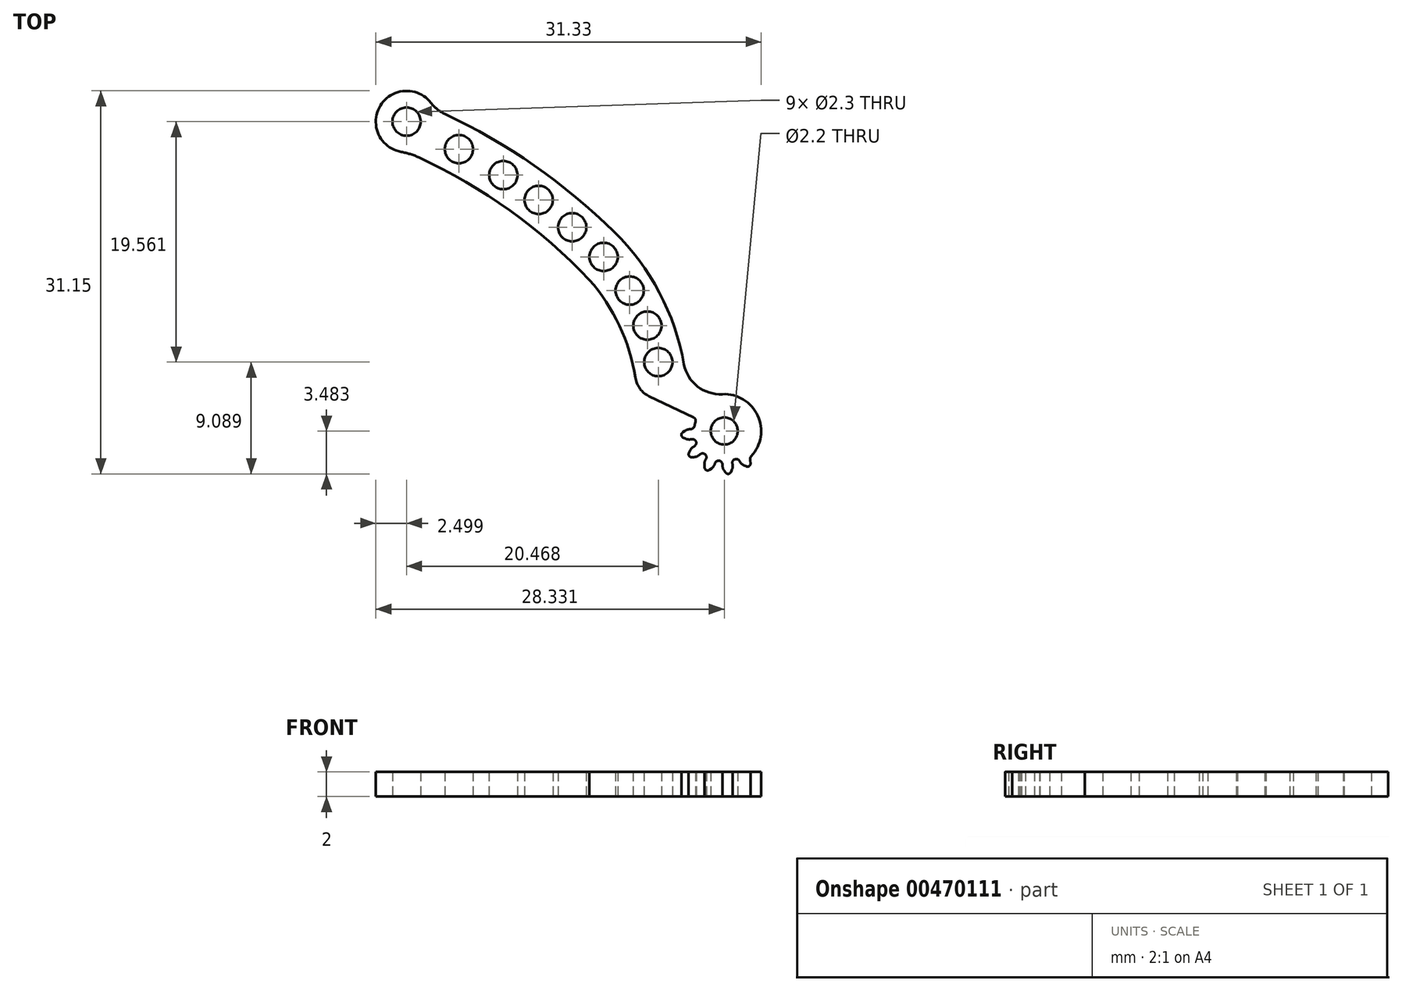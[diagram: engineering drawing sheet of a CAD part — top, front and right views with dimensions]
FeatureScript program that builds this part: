
annotation { "Feature Type Name" : "Feature", "Feature Type Description" : "" }
export const myFeature = defineFeature(function(context is Context, id is Id, definition is map)
    precondition{}
    {
        {
            var Q0;
            Q0=qCreatedBy(makeId("Top.planeOp"),FACE);
            var sketch = newSketch(context, id + "F0", { "sketchPlane" : qUnion([Q0])});
            skCircle(sketch, "E0", {"center": v(1.21, -17.45) * mm, "radius": 1.1 * mm});
            skArc(sketch, "E1", {"start": v(1.58, -20.42) * mm, "mid": v(4.1, -18.23) * mm, "end": v(3.02, -15.06) * mm});
            skArc(sketch, "E2", {"start": v(-0.1, -15.38) * mm, "mid": v(-0.23, -15.47) * mm, "end": v(-0.36, -15.56) * mm});
            skArc(sketch, "E3", {"start": v(4.77, 0.7) * mm, "mid": v(3.26, 9.01) * mm, "end": v(0.37, 16.95) * mm});
            skArc(sketch, "E4", {"start": v(0.1, 18.33) * mm, "mid": v(-3.2, 20.8) * mm, "end": v(-4.32, 16.84) * mm});
            skArc(sketch, "E5", {"start": v(0.1, 18.33) * mm, "mid": v(0.15, 17.62) * mm, "end": v(0.37, 16.95) * mm});
            skArc(sketch, "E6", {"start": v(2.2, -11.17) * mm, "mid": v(4.4, -5.43) * mm, "end": v(4.77, 0.7) * mm});
            skArc(sketch, "E7", {"start": v(2.2, -11.17) * mm, "mid": v(1.88, -13.27) * mm, "end": v(3.02, -15.06) * mm});
            skArc(sketch, "E8", {"start": v(-1.45, -15.36) * mm, "mid": v(-1.57, -15.38) * mm, "end": v(-1.67, -15.46) * mm});
            skArc(sketch, "E9", {"start": v(-0.81, -15.56) * mm, "mid": v(-1.02, -15.43) * mm, "end": v(-1.25, -15.37) * mm});
            skLineSegment(sketch, "E10", {"start": v(-1.25, -15.37) * mm, "end": v(-1.45, -15.36) * mm});
            skArc(sketch, "E11", {"start": v(-0.81, -15.56) * mm, "mid": v(-0.59, -15.64) * mm, "end": v(-0.36, -15.56) * mm});
            skArc(sketch, "E12", {"start": v(-1.67, -15.46) * mm, "mid": v(-1.72, -15.59) * mm, "end": v(-1.7, -15.71) * mm});
            skArc(sketch, "E13", {"start": v(-1.6, -15.9) * mm, "mid": v(-1.46, -16.1) * mm, "end": v(-1.26, -16.25) * mm});
            skLineSegment(sketch, "E14", {"start": v(-1.6, -15.9) * mm, "end": v(-1.7, -15.71) * mm});
            skArc(sketch, "E15", {"start": v(-2.14, -16.97) * mm, "mid": v(-2.23, -17.05) * mm, "end": v(-2.28, -17.17) * mm});
            skArc(sketch, "E16", {"start": v(-1.46, -16.83) * mm, "mid": v(-1.71, -16.81) * mm, "end": v(-1.96, -16.88) * mm});
            skLineSegment(sketch, "E17", {"start": v(-1.96, -16.88) * mm, "end": v(-2.14, -16.97) * mm});
            skArc(sketch, "E18", {"start": v(-2.28, -17.17) * mm, "mid": v(-2.25, -17.3) * mm, "end": v(-2.17, -17.4) * mm});
            skArc(sketch, "E19", {"start": v(-2, -17.51) * mm, "mid": v(-1.78, -17.62) * mm, "end": v(-1.53, -17.64) * mm});
            skLineSegment(sketch, "E20", {"start": v(-2, -17.51) * mm, "end": v(-2.17, -17.4) * mm});
            skArc(sketch, "E21", {"start": v(-1.93, -18.7) * mm, "mid": v(-1.97, -18.83) * mm, "end": v(-1.95, -18.95) * mm});
            skArc(sketch, "E22", {"start": v(-1.41, -18.25) * mm, "mid": v(-1.64, -18.36) * mm, "end": v(-1.82, -18.54) * mm});
            skLineSegment(sketch, "E23", {"start": v(-1.82, -18.54) * mm, "end": v(-1.93, -18.7) * mm});
            skArc(sketch, "E24", {"start": v(-1.95, -18.95) * mm, "mid": v(-1.86, -19.05) * mm, "end": v(-1.74, -19.1) * mm});
            skArc(sketch, "E25", {"start": v(-1.54, -19.11) * mm, "mid": v(-1.3, -19.09) * mm, "end": v(-1.06, -18.98) * mm});
            skLineSegment(sketch, "E26", {"start": v(-1.54, -19.11) * mm, "end": v(-1.74, -19.1) * mm});
            skArc(sketch, "E27", {"start": v(-0.88, -20.1) * mm, "mid": v(-0.86, -20.23) * mm, "end": v(-0.77, -20.33) * mm});
            skArc(sketch, "E28", {"start": v(-0.66, -19.45) * mm, "mid": v(-0.8, -19.66) * mm, "end": v(-0.86, -19.9) * mm});
            skLineSegment(sketch, "E29", {"start": v(-0.86, -19.9) * mm, "end": v(-0.88, -20.1) * mm});
            skArc(sketch, "E30", {"start": v(-0.77, -20.33) * mm, "mid": v(-0.65, -20.37) * mm, "end": v(-0.52, -20.35) * mm});
            skArc(sketch, "E31", {"start": v(-0.34, -20.27) * mm, "mid": v(-0.14, -20.12) * mm, "end": v(0.01, -19.91) * mm});
            skLineSegment(sketch, "E32", {"start": v(-0.34, -20.27) * mm, "end": v(-0.52, -20.35) * mm});
            skArc(sketch, "E33", {"start": v(0.73, -20.8) * mm, "mid": v(0.81, -20.9) * mm, "end": v(0.94, -20.94) * mm});
            skArc(sketch, "E34", {"start": v(0.6, -20.12) * mm, "mid": v(0.58, -20.37) * mm, "end": v(0.64, -20.61) * mm});
            skLineSegment(sketch, "E35", {"start": v(0.64, -20.61) * mm, "end": v(0.73, -20.8) * mm});
            skArc(sketch, "E36", {"start": v(0.94, -20.94) * mm, "mid": v(1.06, -20.91) * mm, "end": v(1.16, -20.83) * mm});
            skArc(sketch, "E37", {"start": v(1.28, -20.66) * mm, "mid": v(1.3, -20.63) * mm, "end": v(1.31, -20.6) * mm});
            skLineSegment(sketch, "E38", {"start": v(1.28, -20.66) * mm, "end": v(1.16, -20.83) * mm});
            skArc(sketch, "E39", {"start": v(1.58, -20.42) * mm, "mid": v(1.42, -20.48) * mm, "end": v(1.31, -20.6) * mm});
            skArc(sketch, "E40", {"start": v(0.6, -20.12) * mm, "mid": v(0.4, -19.76) * mm, "end": v(0.01, -19.91) * mm});
            skArc(sketch, "E41", {"start": v(-0.66, -19.45) * mm, "mid": v(-0.65, -19.04) * mm, "end": v(-1.06, -18.98) * mm});
            skArc(sketch, "E42", {"start": v(-1.41, -18.25) * mm, "mid": v(-1.2, -17.9) * mm, "end": v(-1.53, -17.64) * mm});
            skArc(sketch, "E43", {"start": v(-1.46, -16.83) * mm, "mid": v(-1.1, -16.63) * mm, "end": v(-1.26, -16.25) * mm});
            skCircle(sketch, "E44", {"center": v(-2.4, 18.44) * mm, "radius": 1.15 * mm});
            skLineSegment(sketch, "E45", {"start": v(0, -15) * mm, "end": v(-1.65, -11.36) * mm});
            skArc(sketch, "E46", {"start": v(-0.1, -15.38) * mm, "mid": v(0.02, -15.2) * mm, "end": v(0, -15) * mm});
            skArc(sketch, "E47", {"start": v(-1.53, -9.49) * mm, "mid": v(0.2, -5.4) * mm, "end": v(0.72, -1) * mm});
            skArc(sketch, "E48", {"start": v(-1.53, -9.49) * mm, "mid": v(-1.82, -10.41) * mm, "end": v(-1.65, -11.36) * mm});
            skArc(sketch, "E49", {"start": v(0.72, -1) * mm, "mid": v(-0.62, 7.48) * mm, "end": v(-3.5, 15.56) * mm});
            skArc(sketch, "E50", {"start": v(-3.5, 15.56) * mm, "mid": v(-3.87, 16.22) * mm, "end": v(-4.32, 16.84) * mm});
            skCircle(sketch, "E51", {"center": v(0.7, -9.7) * mm, "radius": 1.15 * mm});
            skCircle(sketch, "E52", {"center": v(1.93, -6.86) * mm, "radius": 1.15 * mm});
            skCircle(sketch, "E53", {"center": v(2.67, -3.75) * mm, "radius": 1.15 * mm});
            skCircle(sketch, "E54", {"center": v(2.8, -0.3) * mm, "radius": 1.15 * mm});
            skCircle(sketch, "E55", {"center": v(2.4, 3.2) * mm, "radius": 1.15 * mm});
            skCircle(sketch, "E56", {"center": v(1.74, 6.65) * mm, "radius": 1.15 * mm});
            skCircle(sketch, "E57", {"center": v(0.83, 10.05) * mm, "radius": 1.15 * mm});
            skCircle(sketch, "E58", {"center": v(-0.58, 13.99) * mm, "radius": 1.15 * mm});
            skSolve(sketch);
        }
        {
            var Q0;
            Q0 = qSketchRegion(id + "F0", true);
            extrude(context, id + "F1", {"entities" : qUnion([Q0]), "depth" : 2 * mm});
        }
        {
            var Q0;
            Q0=makeQuery(id+"F1.opExtrude","SWEPT_BODY",BODY,{"disambiguationData":[OSD([sQuery(id+"F0.wireOp",EDGE,"E0"),sQuery(id+"F0.wireOp",EDGE,"E1"),sQuery(id+"F0.wireOp",EDGE,"E2"),sQuery(id+"F0.wireOp",EDGE,"E3"),sQuery(id+"F0.wireOp",EDGE,"E4"),sQuery(id+"F0.wireOp",EDGE,"E5"),sQuery(id+"F0.wireOp",EDGE,"E6"),sQuery(id+"F0.wireOp",EDGE,"E7"),sQuery(id+"F0.wireOp",EDGE,"E8"),sQuery(id+"F0.wireOp",EDGE,"E9"),sQuery(id+"F0.wireOp",EDGE,"E10"),sQuery(id+"F0.wireOp",EDGE,"E11"),sQuery(id+"F0.wireOp",EDGE,"E12"),sQuery(id+"F0.wireOp",EDGE,"E13"),sQuery(id+"F0.wireOp",EDGE,"E14"),sQuery(id+"F0.wireOp",EDGE,"E15"),sQuery(id+"F0.wireOp",EDGE,"E16"),sQuery(id+"F0.wireOp",EDGE,"E17"),sQuery(id+"F0.wireOp",EDGE,"E18"),sQuery(id+"F0.wireOp",EDGE,"E19"),sQuery(id+"F0.wireOp",EDGE,"E20"),sQuery(id+"F0.wireOp",EDGE,"E21"),sQuery(id+"F0.wireOp",EDGE,"E22"),sQuery(id+"F0.wireOp",EDGE,"E23"),sQuery(id+"F0.wireOp",EDGE,"E24"),sQuery(id+"F0.wireOp",EDGE,"E25"),sQuery(id+"F0.wireOp",EDGE,"E26"),sQuery(id+"F0.wireOp",EDGE,"E27"),sQuery(id+"F0.wireOp",EDGE,"E28"),sQuery(id+"F0.wireOp",EDGE,"E29"),sQuery(id+"F0.wireOp",EDGE,"E30"),sQuery(id+"F0.wireOp",EDGE,"E31"),sQuery(id+"F0.wireOp",EDGE,"E32"),sQuery(id+"F0.wireOp",EDGE,"E33"),sQuery(id+"F0.wireOp",EDGE,"E34"),sQuery(id+"F0.wireOp",EDGE,"E35"),sQuery(id+"F0.wireOp",EDGE,"E36"),sQuery(id+"F0.wireOp",EDGE,"E37"),sQuery(id+"F0.wireOp",EDGE,"E38"),sQuery(id+"F0.wireOp",EDGE,"E39"),sQuery(id+"F0.wireOp",EDGE,"E40"),sQuery(id+"F0.wireOp",EDGE,"E41"),sQuery(id+"F0.wireOp",EDGE,"E42"),sQuery(id+"F0.wireOp",EDGE,"E43"),sQuery(id+"F0.wireOp",EDGE,"E44"),sQuery(id+"F0.wireOp",EDGE,"E45"),sQuery(id+"F0.wireOp",EDGE,"E46"),sQuery(id+"F0.wireOp",EDGE,"E47"),sQuery(id+"F0.wireOp",EDGE,"E48"),sQuery(id+"F0.wireOp",EDGE,"E49"),sQuery(id+"F0.wireOp",EDGE,"E50"),sQuery(id+"F0.wireOp",EDGE,"E51"),sQuery(id+"F0.wireOp",EDGE,"E52"),sQuery(id+"F0.wireOp",EDGE,"E53"),sQuery(id+"F0.wireOp",EDGE,"E54"),sQuery(id+"F0.wireOp",EDGE,"E55"),sQuery(id+"F0.wireOp",EDGE,"E56"),sQuery(id+"F0.wireOp",EDGE,"E57"),sQuery(id+"F0.wireOp",EDGE,"E58")])]});
            var Q1;
            Q1=makeQuery(id+"F1.opExtrude","CAP_EDGE",EDGE,{"disambiguationData":[OSD([sQuery(id+"F0.wireOp",EDGE,"E0")])],"isStart":false});
            var Q2;
            Q2=makeQuery(id+"F1.opExtrude","CAP_EDGE",EDGE,{"disambiguationData":[OSD([sQuery(id+"F0.wireOp",EDGE,"E0")])],"isStart":false});
            transform(context, id + "F2", {"entities" : qUnion([Q0]), "transformType" : TransformType.ROTATION, "transformAxis" : qUnion([Q2]), "angle" : 40 * degree, "makeCopy" : false});
        }
    });
